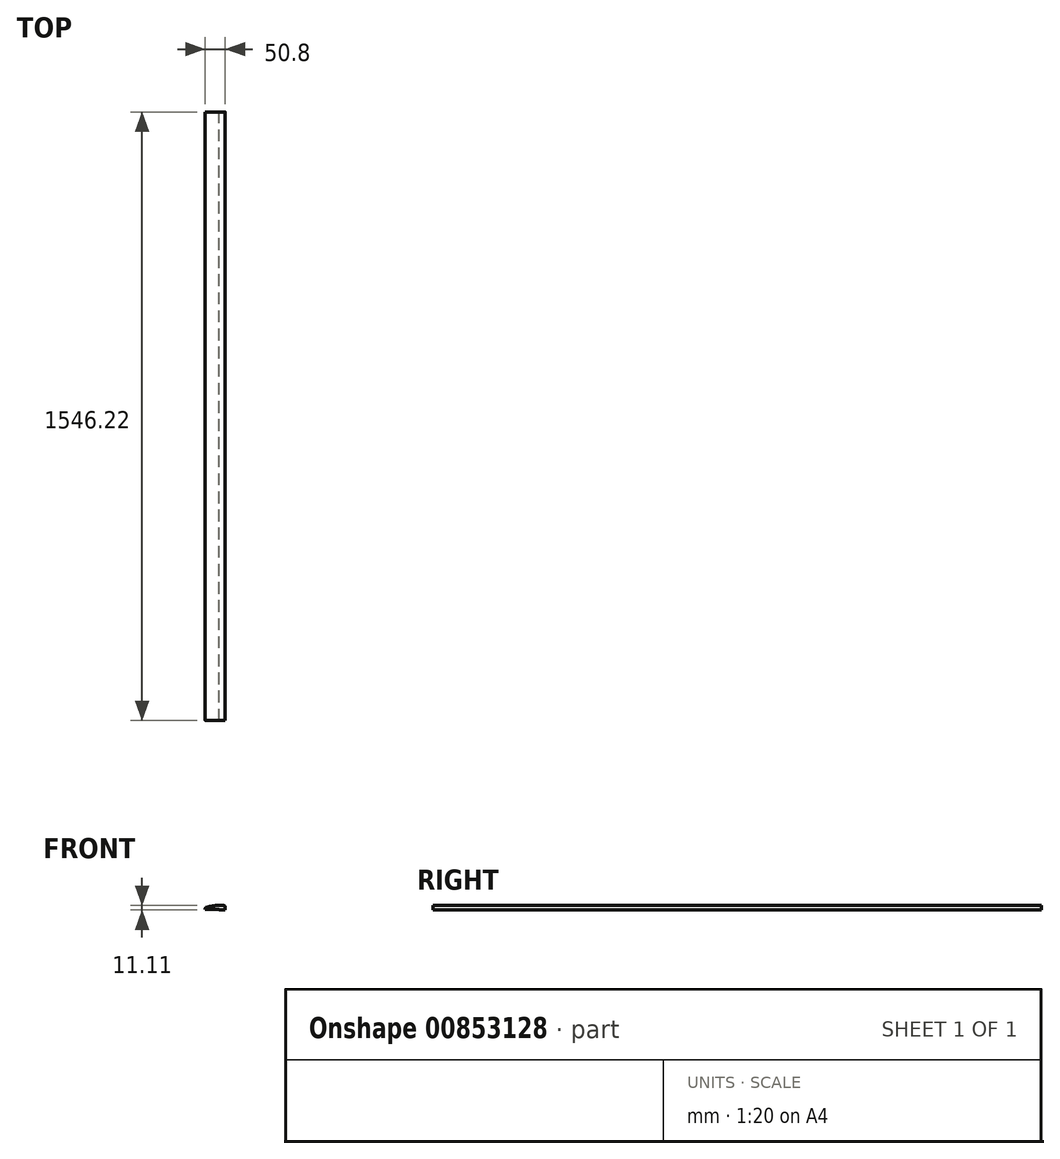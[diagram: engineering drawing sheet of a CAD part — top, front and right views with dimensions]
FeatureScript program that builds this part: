
annotation { "Feature Type Name" : "Feature", "Feature Type Description" : "" }
export const myFeature = defineFeature(function(context is Context, id is Id, definition is map)
    precondition{}
    {
        {
            var Q0;
            Q0=qCreatedBy(makeId("Front.planeOp"),FACE);
            var sketch = newSketch(context, id + "F0", { "sketchPlane" : qUnion([Q0])});
            skLineSegment(sketch, "E0", {"start": v(-31.68, 5.56) * mm, "end": v(-31.68, 1.59) * mm});
            skLineSegment(sketch, "E1", {"start": v(3.25, 0) * mm, "end": v(19.12, 0) * mm});
            skLineSegment(sketch, "E2", {"start": v(19.12, 0) * mm, "end": v(19.12, 11.11) * mm});
            skLineSegment(sketch, "E3", {"start": v(-31.68, 5.56) * mm, "end": v(-10.95, 11.11) * mm});
            skLineSegment(sketch, "E4", {"start": v(-10.95, 11.11) * mm, "end": v(19.12, 11.11) * mm});
            skLineSegment(sketch, "E5", {"start": v(-31.68, 1.59) * mm, "end": v(3.25, 1.59) * mm});
            skLineSegment(sketch, "E6", {"start": v(3.25, 0) * mm, "end": v(3.25, 1.59) * mm});
            skSolve(sketch);
        }
        {
            var Q0;
            Q0 = qSketchRegion(id + "F0", true);
            extrude(context, id + "F1", {"entities" : qUnion([Q0]), "depth" : 1546.22 * mm, "offsetDistance" : 25.4 * mm});
        }
        {
            var Q0;
            Q0=makeQuery(id+"F1.opExtrude","SWEPT_EDGE",EDGE,{"disambiguationData":[OSD([sQuery(id+"F0.wireOp",EDGE,"E3"),sQuery(id+"F0.wireOp",EDGE,"E4")])]});
            fillet(context, id + "F2", {"entities" : qUnion([Q0]), "radius" : 76.2 * mm, "tangentPropagation" : true, "allowEdgeOverflow" : false});
        }
        {
            var Q0;
            Q0=makeQuery(id+"F1.opExtrude","SWEPT_EDGE",EDGE,{"disambiguationData":[OSD([sQuery(id+"F0.wireOp",EDGE,"E0"),sQuery(id+"F0.wireOp",EDGE,"E3")])]});
            fillet(context, id + "F3", {"entities" : qUnion([Q0]), "radius" : 3.17 * mm, "tangentPropagation" : true, "allowEdgeOverflow" : false});
        }
        {
            var Q0;
            Q0=makeQuery(id+"F1.opExtrude","SWEPT_EDGE",EDGE,{"disambiguationData":[OSD([sQuery(id+"F0.wireOp",EDGE,"E2"),sQuery(id+"F0.wireOp",EDGE,"E4")])]});
            fillet(context, id + "F4", {"entities" : qUnion([Q0]), "radius" : 3.17 * mm, "tangentPropagation" : true, "allowEdgeOverflow" : false});
        }
    });
